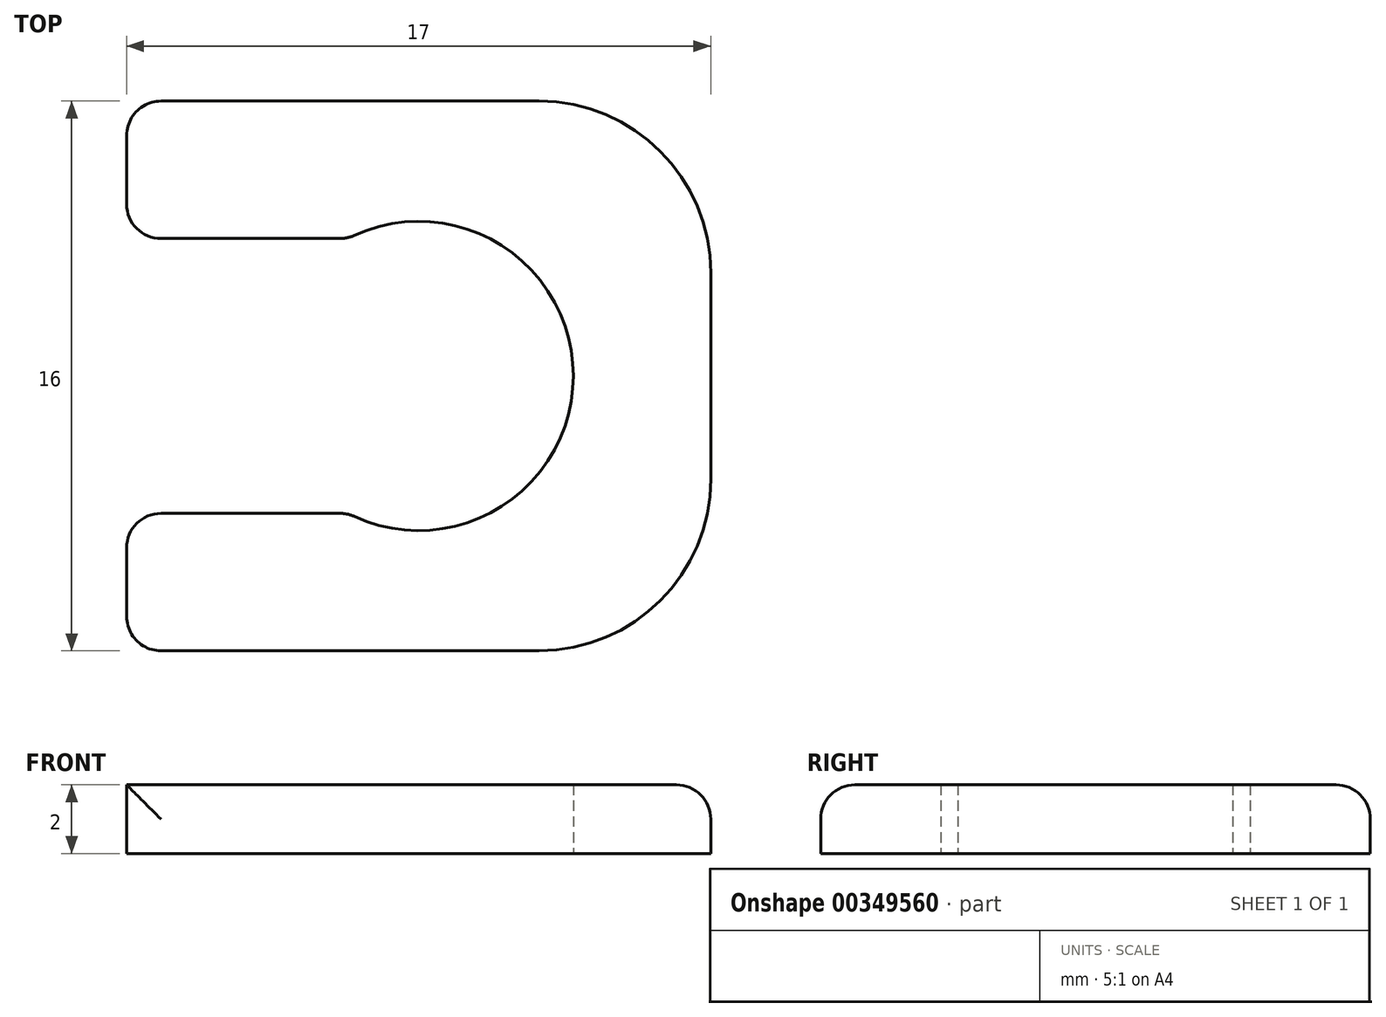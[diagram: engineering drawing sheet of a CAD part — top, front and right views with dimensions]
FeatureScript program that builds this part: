
annotation { "Feature Type Name" : "Feature", "Feature Type Description" : "" }
export const myFeature = defineFeature(function(context is Context, id is Id, definition is map)
    precondition{}
    {
        {
            var Q0;
            Q0=qCreatedBy(makeId("Top.planeOp"),FACE);
            var sketch = newSketch(context, id + "F0", { "sketchPlane" : qUnion([Q0])});
            skLineSegment(sketch, "E0.bottom", {"start": v(-8.5, 8) * mm, "end": v(8.5, 8) * mm});
            skLineSegment(sketch, "E0.top", {"start": v(-8.5, -8) * mm, "end": v(8.5, -8) * mm});
            skLineSegment(sketch, "E0.left", {"start": v(-8.5, 8) * mm, "end": v(-8.5, -8) * mm});
            skLineSegment(sketch, "E0.right", {"start": v(8.5, 8) * mm, "end": v(8.5, -8) * mm});
            skPoint(sketch, "E0.middle", {"position": v(0, 0) * mm});
            skCircle(sketch, "E1", {"center": v(0, 0) * mm, "radius": 4.5 * mm});
            skLineSegment(sketch, "E2", {"start": v(0, 4.5) * mm, "end": v(-8.5, 4.5) * mm});
            skLineSegment(sketch, "E3", {"start": v(0, -4.5) * mm, "end": v(-8.5, -4.5) * mm});
            skLineSegment(sketch, "E4", {"start": v(-8.5, 4) * mm, "end": v(-2.06, 4) * mm});
            skLineSegment(sketch, "E5", {"start": v(-8.5, -4) * mm, "end": v(-2.06, -4) * mm});
            skSolve(sketch);
        }
        {
            var Q0;
            {var subQ3=sQuery(id+"F0.wireOp",EDGE,"E0.bottom");Q0=makeQuery(id+"F0.imprint","IMPRINT",FACE,{"disambiguationData":[TD([[makeQuery(id+"F0.imprint","IMPRINT",EDGE,{"derivedFrom":subQ3}),-1.0]])]});}
            var Q1;
            {var subQ0=sQuery(id+"F0.wireOp",EDGE,"E2");Q1=makeQuery(id+"F0.imprint","IMPRINT",FACE,{"disambiguationData":[TD([[makeQuery(id+"F0.imprint","IMPRINT",EDGE,{"derivedFrom":subQ0}),1.0]])]});}
            var Q2;
            {var subQ0=sQuery(id+"F0.wireOp",EDGE,"E3");Q2=makeQuery(id+"F0.imprint","IMPRINT",FACE,{"disambiguationData":[TD([[makeQuery(id+"F0.imprint","IMPRINT",EDGE,{"derivedFrom":subQ0}),-1.0]])]});}
            extrude(context, id + "F1", {"entities" : qUnion([Q0, Q1, Q2]), "depth" : 2 * mm, "offsetDistance" : 25 * mm});
        }
        {
            var Q0;
            Q0=makeQuery(id+"F1.opExtrude","SWEPT_EDGE",EDGE,{"disambiguationData":[OSD([sQuery(id+"F0.wireOp",EDGE,"E0.bottom"),sQuery(id+"F0.wireOp",EDGE,"E0.right")])]});
            var Q1;
            Q1=makeQuery(id+"F1.opExtrude","SWEPT_EDGE",EDGE,{"disambiguationData":[OSD([sQuery(id+"F0.wireOp",EDGE,"E0.top"),sQuery(id+"F0.wireOp",EDGE,"E0.right")])]});
            fillet(context, id + "F2", {"entities" : qUnion([Q0, Q1]), "radius" : 5 * mm, "tangentPropagation" : true, "allowEdgeOverflow" : false});
        }
        {
            var Q0;
            Q0=makeQuery(id+"F1.opExtrude","SWEPT_EDGE",EDGE,{"disambiguationData":[OSD([sQuery(id+"F0.wireOp",EDGE,"E1"),sQuery(id+"F0.wireOp",EDGE,"E5")])]});
            var Q1;
            Q1=makeQuery(id+"F1.opExtrude","SWEPT_EDGE",EDGE,{"disambiguationData":[OSD([sQuery(id+"F0.wireOp",EDGE,"E1"),sQuery(id+"F0.wireOp",EDGE,"E4")])]});
            var Q2;
            Q2=makeQuery(id+"F1.opExtrude","CAP_EDGE",EDGE,{"disambiguationData":[OSD([sQuery(id+"F0.wireOp",EDGE,"E0.bottom")])],"isStart":false});
            var Q3;
            Q3=makeQuery(id+"F1.opExtrude","SWEPT_EDGE",EDGE,{"disambiguationData":[OSD([sQuery(id+"F0.wireOp",EDGE,"E0.left"),sQuery(id+"F0.wireOp",EDGE,"E5")])]});
            var Q4;
            Q4=makeQuery(id+"F1.opExtrude","SWEPT_EDGE",EDGE,{"disambiguationData":[OSD([sQuery(id+"F0.wireOp",EDGE,"E0.top"),sQuery(id+"F0.wireOp",EDGE,"E0.left")])]});
            var Q5;
            Q5=makeQuery(id+"F1.opExtrude","SWEPT_EDGE",EDGE,{"disambiguationData":[OSD([sQuery(id+"F0.wireOp",EDGE,"E0.left"),sQuery(id+"F0.wireOp",EDGE,"E4")])]});
            var Q6;
            Q6=makeQuery(id+"F1.opExtrude","SWEPT_EDGE",EDGE,{"disambiguationData":[OSD([sQuery(id+"F0.wireOp",EDGE,"E0.bottom"),sQuery(id+"F0.wireOp",EDGE,"E0.left")])]});
            fillet(context, id + "F3", {"entities" : qUnion([Q0, Q1, Q2, Q3, Q4, Q5, Q6]), "radius" : 1 * mm, "tangentPropagation" : true, "allowEdgeOverflow" : false});
        }
    });
